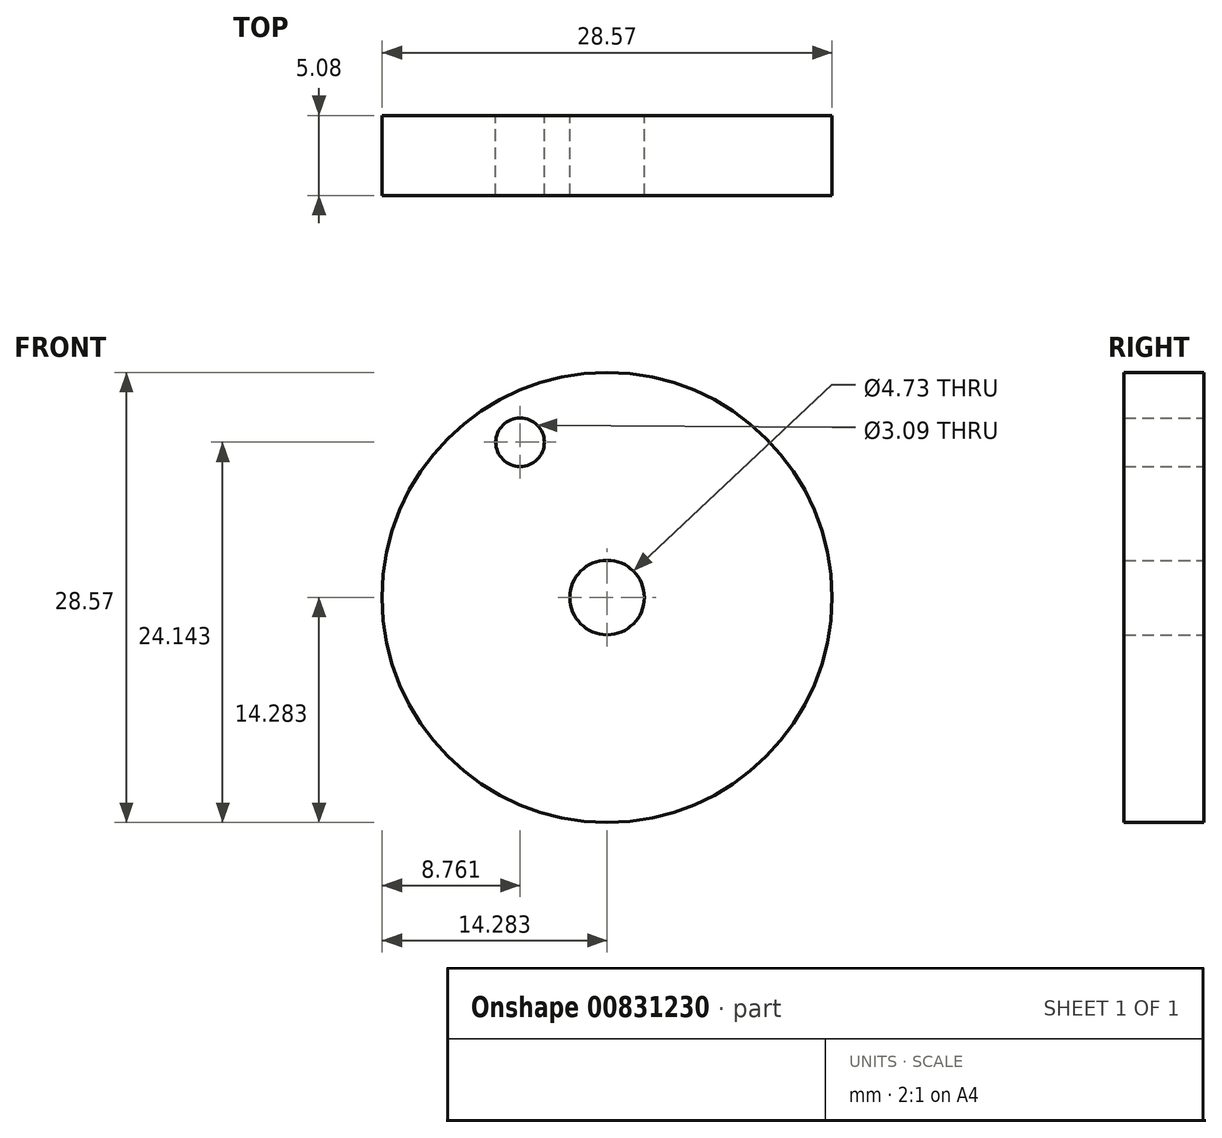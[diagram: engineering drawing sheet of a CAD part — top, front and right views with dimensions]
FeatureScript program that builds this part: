
annotation { "Feature Type Name" : "Feature", "Feature Type Description" : "" }
export const myFeature = defineFeature(function(context is Context, id is Id, definition is map)
    precondition{}
    {
        {
            var Q0;
            Q0=qCreatedBy(makeId("Front.planeOp"),FACE);
            var sketch = newSketch(context, id + "F0", { "sketchPlane" : qUnion([Q0])});
            skCircle(sketch, "E0", {"center": v(-58.34, 39.01) * mm, "radius": 14.29 * mm});
            skCircle(sketch, "E1", {"center": v(-58.34, 39.01) * mm, "radius": 2.37 * mm});
            skCircle(sketch, "E2", {"center": v(-63.86, 48.87) * mm, "radius": 1.54 * mm});
            skSolve(sketch);
        }
        {
            var Q0;
            Q0=makeQuery(id+"F0.imprint","IMPRINT",FACE,{"disambiguationData":[TD([[makeQuery(id+"F0.imprint","IMPRINT",EDGE,{"derivedFrom":sQuery(id+"F0.wireOp",EDGE,"E0")}),1.0]])]});
            extrude(context, id + "F1", {"entities" : qUnion([Q0]), "depth" : 5.08 * mm, "offsetDistance" : 25.4 * mm});
        }
    });
